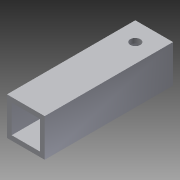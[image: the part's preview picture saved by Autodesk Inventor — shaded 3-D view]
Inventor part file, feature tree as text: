
AUTODESK INVENTOR PART (.ipt)
format: ipt  version: 2014 SP1 (Build 180222100, 222)  size: 90,624 bytes
history: native  units: in
note: dims shown in document units (in); Inventor stores cm internally (conversion verified against a paired STEP export)
features: extrude x2, sketch x2
ambient origin geometry x8: Origin, YZ Plane, XZ Plane, XY Plane, X Axis, Y Axis, Z Axis, Center Point
bodies: Solid1 (feature_tree)
feature tree (4):
  extrude  "Extrusion1"  Depth=1.0in
  extrude  "Extrusion2"  Depth=3.4in TaperAngle=0.0deg
  sketch  "Sketch1"  dims[d0=1.0in d1=1.0in]
  sketch  "Sketch2"  dims[d2=0.125in d3=3.4in d4=0.0in d5=0.5in d6=0.266in d7=3.4in d8=0.0in]
